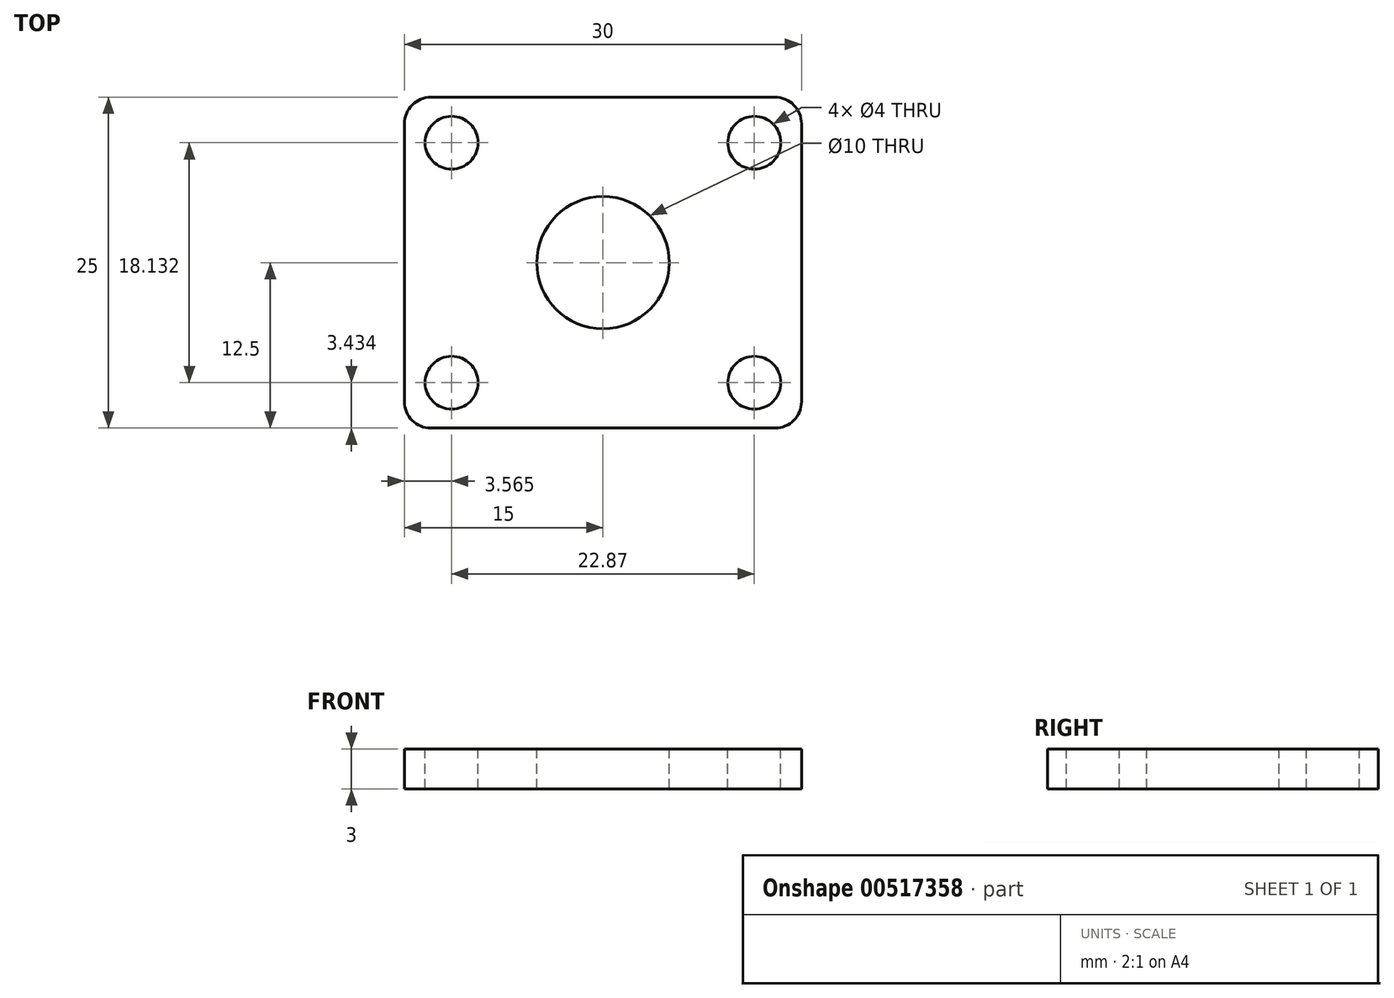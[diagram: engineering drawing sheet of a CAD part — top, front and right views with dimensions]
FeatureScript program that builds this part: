
annotation { "Feature Type Name" : "Feature", "Feature Type Description" : "" }
export const myFeature = defineFeature(function(context is Context, id is Id, definition is map)
    precondition{}
    {
        {
            var Q0;
            Q0=qCreatedBy(makeId("Top.planeOp"),FACE);
            var sketch = newSketch(context, id + "F0", { "sketchPlane" : qUnion([Q0])});
            skLineSegment(sketch, "E0.bottom", {"start": v(15, 12.5) * mm, "end": v(-15, 12.5) * mm});
            skLineSegment(sketch, "E0.top", {"start": v(15, -12.5) * mm, "end": v(-15, -12.5) * mm});
            skLineSegment(sketch, "E0.left", {"start": v(15, 12.5) * mm, "end": v(15, -12.5) * mm});
            skLineSegment(sketch, "E0.right", {"start": v(-15, 12.5) * mm, "end": v(-15, -12.5) * mm});
            skPoint(sketch, "E0.middle", {"position": v(0, 0) * mm});
            skSolve(sketch);
        }
        {
            var Q0;
            Q0 = qSketchRegion(id + "F0", true);
            extrude(context, id + "F1", {"entities" : qUnion([Q0]), "depth" : 3 * mm, "offsetDistance" : 25 * mm});
        }
        {
            var Q0;
            Q0=makeQuery(id+"F1.opExtrude","SWEPT_EDGE",EDGE,{"disambiguationData":[OSD([sQuery(id+"F0.wireOp",EDGE,"E0.bottom"),sQuery(id+"F0.wireOp",EDGE,"E0.left")])]});
            var Q1;
            Q1=makeQuery(id+"F1.opExtrude","SWEPT_EDGE",EDGE,{"disambiguationData":[OSD([sQuery(id+"F0.wireOp",EDGE,"E0.bottom"),sQuery(id+"F0.wireOp",EDGE,"E0.right")])]});
            var Q2;
            Q2=makeQuery(id+"F1.opExtrude","SWEPT_EDGE",EDGE,{"disambiguationData":[OSD([sQuery(id+"F0.wireOp",EDGE,"E0.top"),sQuery(id+"F0.wireOp",EDGE,"E0.right")])]});
            var Q3;
            Q3=makeQuery(id+"F1.opExtrude","SWEPT_EDGE",EDGE,{"disambiguationData":[OSD([sQuery(id+"F0.wireOp",EDGE,"E0.top"),sQuery(id+"F0.wireOp",EDGE,"E0.left")])]});
            fillet(context, id + "F2", {"entities" : qUnion([Q0, Q1, Q2, Q3]), "tangentPropagation" : true, "radius" : 2 * mm, "defaultsChanged" : false, "vertexSettings" : [], "allowEdgeOverflow" : false});
        }
        {
            var Q0;
            Q0=makeQuery(id+"F1.opExtrude","CAP_FACE",FACE,{"disambiguationData":[OSD([sQuery(id+"F0.wireOp",EDGE,"E0.bottom"),sQuery(id+"F0.wireOp",EDGE,"E0.top"),sQuery(id+"F0.wireOp",EDGE,"E0.left"),sQuery(id+"F0.wireOp",EDGE,"E0.right")])],"isStart":false});
            var sketch = newSketch(context, id + "F3", { "sketchPlane" : qUnion([Q0])});
            skCircle(sketch, "E1", {"center": v(0, 0) * mm, "radius": 5 * mm});
            skSolve(sketch);
        }
        {
            var Q0;
            Q0 = qSketchRegion(id + "F3", true);
            extrude(context, id + "F4", {"entities" : qUnion([Q0]), "operationType" : NewBodyOperationType.REMOVE, "oppositeDirection" : true, "depth" : 3 * mm, "offsetDistance" : 25 * mm});
        }
        {
            var Q0;
            Q0=makeQuery(id+"F1.opExtrude","CAP_FACE",FACE,{"disambiguationData":[OSD([sQuery(id+"F0.wireOp",EDGE,"E0.bottom"),sQuery(id+"F0.wireOp",EDGE,"E0.top"),sQuery(id+"F0.wireOp",EDGE,"E0.left"),sQuery(id+"F0.wireOp",EDGE,"E0.right")])],"isStart":false});
            var sketch = newSketch(context, id + "F5", { "sketchPlane" : qUnion([Q0])});
            skCircle(sketch, "E2", {"center": v(-11.43, 9.07) * mm, "radius": 2 * mm});
            skCircle(sketch, "E3.MirrorC", {"center": v(11.43, 9.07) * mm, "radius": 2 * mm});
            skCircle(sketch, "E4.MirrorC", {"center": v(-11.43, -9.07) * mm, "radius": 2 * mm});
            skCircle(sketch, "E5.MirrorC", {"center": v(11.43, -9.07) * mm, "radius": 2 * mm});
            skSolve(sketch);
        }
        {
            var Q0;
            Q0 = qSketchRegion(id + "F5", true);
            extrude(context, id + "F6", {"entities" : qUnion([Q0]), "operationType" : NewBodyOperationType.REMOVE, "oppositeDirection" : true, "depth" : 3 * mm, "offsetDistance" : 25 * mm});
        }
    });
